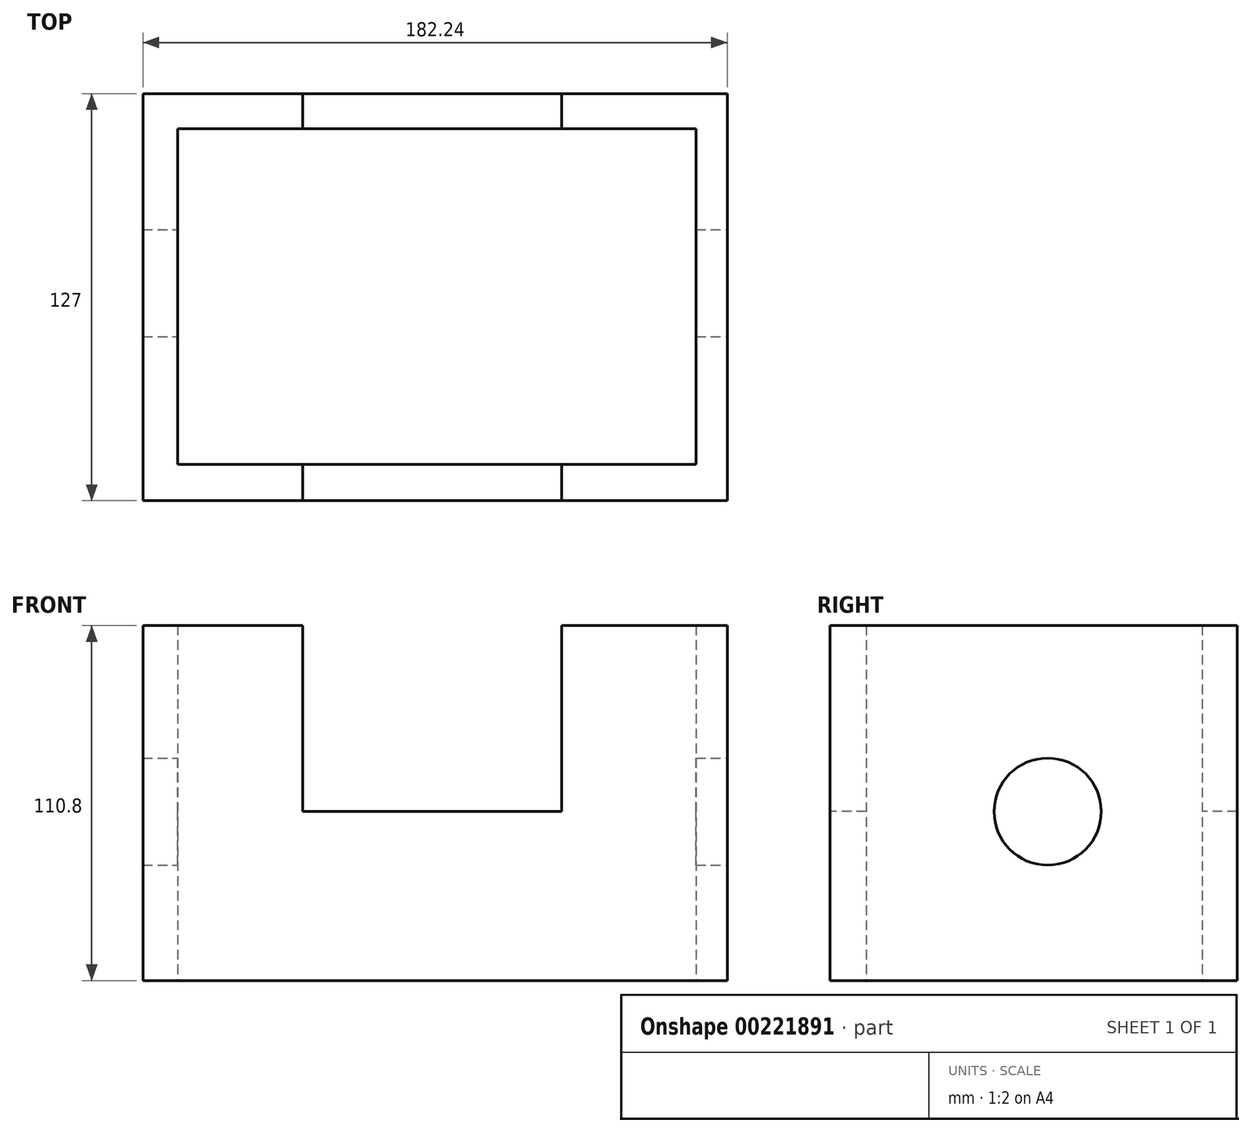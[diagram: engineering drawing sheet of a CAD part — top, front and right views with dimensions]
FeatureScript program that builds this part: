
annotation { "Feature Type Name" : "Feature", "Feature Type Description" : "" }
export const myFeature = defineFeature(function(context is Context, id is Id, definition is map)
    precondition{}
    {
        {
            var Q0;
            Q0=qCreatedBy(makeId("Front.planeOp"),FACE);
            var sketch = newSketch(context, id + "F0", { "sketchPlane" : qUnion([Q0])});
            skLineSegment(sketch, "E0.bottom", {"start": v(-86.34, 58.07) * mm, "end": v(95.9, 58.07) * mm});
            skLineSegment(sketch, "E0.top", {"start": v(-86.34, -52.73) * mm, "end": v(95.9, -52.73) * mm});
            skLineSegment(sketch, "E0.left", {"start": v(-86.34, 58.07) * mm, "end": v(-86.34, -52.73) * mm});
            skLineSegment(sketch, "E0.right", {"start": v(95.9, 58.07) * mm, "end": v(95.9, -52.73) * mm});
            skSolve(sketch);
        }
        {
            var Q0;
            Q0 = qSketchRegion(id + "F0", true);
            extrude(context, id + "F1", {"entities" : qUnion([Q0]), "oppositeDirection" : true, "depth" : 127 * mm});
        }
        {
            var Q0;
            Q0=qCreatedBy(makeId("Front.planeOp"),FACE);
            var sketch = newSketch(context, id + "F2", { "sketchPlane" : qUnion([Q0])});
            skLineSegment(sketch, "E1.bottom", {"start": v(-36.57, 63.7) * mm, "end": v(44.2, 63.7) * mm});
            skLineSegment(sketch, "E1.top", {"start": v(-36.57, 0) * mm, "end": v(44.2, 0) * mm});
            skLineSegment(sketch, "E1.left", {"start": v(-36.57, 63.7) * mm, "end": v(-36.57, 0) * mm});
            skLineSegment(sketch, "E1.right", {"start": v(44.2, 63.7) * mm, "end": v(44.2, 0) * mm});
            skSolve(sketch);
        }
        {
            var Q0;
            Q0 = qSketchRegion(id + "F2", true);
            extrude(context, id + "F3", {"entities" : qUnion([Q0]), "operationType" : NewBodyOperationType.REMOVE, "endBound" : BoundingType.THROUGH_ALL, "oppositeDirection" : true, "depth" : 203.2 * mm});
        }
        {
            var Q0;
            Q0=makeQuery(id+"F1.opExtrude","SWEPT_FACE",FACE,{"disambiguationData":[OSD([sQuery(id+"F0.wireOp",EDGE,"E0.top")])]});
            var sketch = newSketch(context, id + "F4", { "sketchPlane" : qUnion([Q0])});
            skLineSegment(sketch, "E2.bottom", {"start": v(-75.55, -11.33) * mm, "end": v(86.18, -11.33) * mm});
            skLineSegment(sketch, "E2.top", {"start": v(-75.55, -116.1) * mm, "end": v(86.18, -116.1) * mm});
            skLineSegment(sketch, "E2.left", {"start": v(-75.55, -11.33) * mm, "end": v(-75.55, -116.1) * mm});
            skLineSegment(sketch, "E2.right", {"start": v(86.18, -11.33) * mm, "end": v(86.18, -116.1) * mm});
            skPoint(sketch, "E2.middle", {"position": v(5.31, -63.72) * mm});
            skSolve(sketch);
        }
        {
            var Q0;
            Q0 = qSketchRegion(id + "F4", true);
            extrude(context, id + "F5", {"entities" : qUnion([Q0]), "operationType" : NewBodyOperationType.REMOVE, "endBound" : BoundingType.THROUGH_ALL, "oppositeDirection" : true, "depth" : 254 * mm});
        }
        {
            var Q0;
            Q0=makeQuery(id+"F1.opExtrude","SWEPT_FACE",FACE,{"disambiguationData":[OSD([sQuery(id+"F0.wireOp",EDGE,"E0.right")])]});
            var sketch = newSketch(context, id + "F6", { "sketchPlane" : qUnion([Q0])});
            skCircle(sketch, "E3", {"center": v(67.92, 0) * mm, "radius": 16.7 * mm});
            skSolve(sketch);
        }
        {
            var Q0;
            Q0 = qSketchRegion(id + "F6", true);
            extrude(context, id + "F7", {"entities" : qUnion([Q0]), "operationType" : NewBodyOperationType.REMOVE, "endBound" : BoundingType.THROUGH_ALL, "oppositeDirection" : true, "depth" : 254 * mm});
        }
    });
